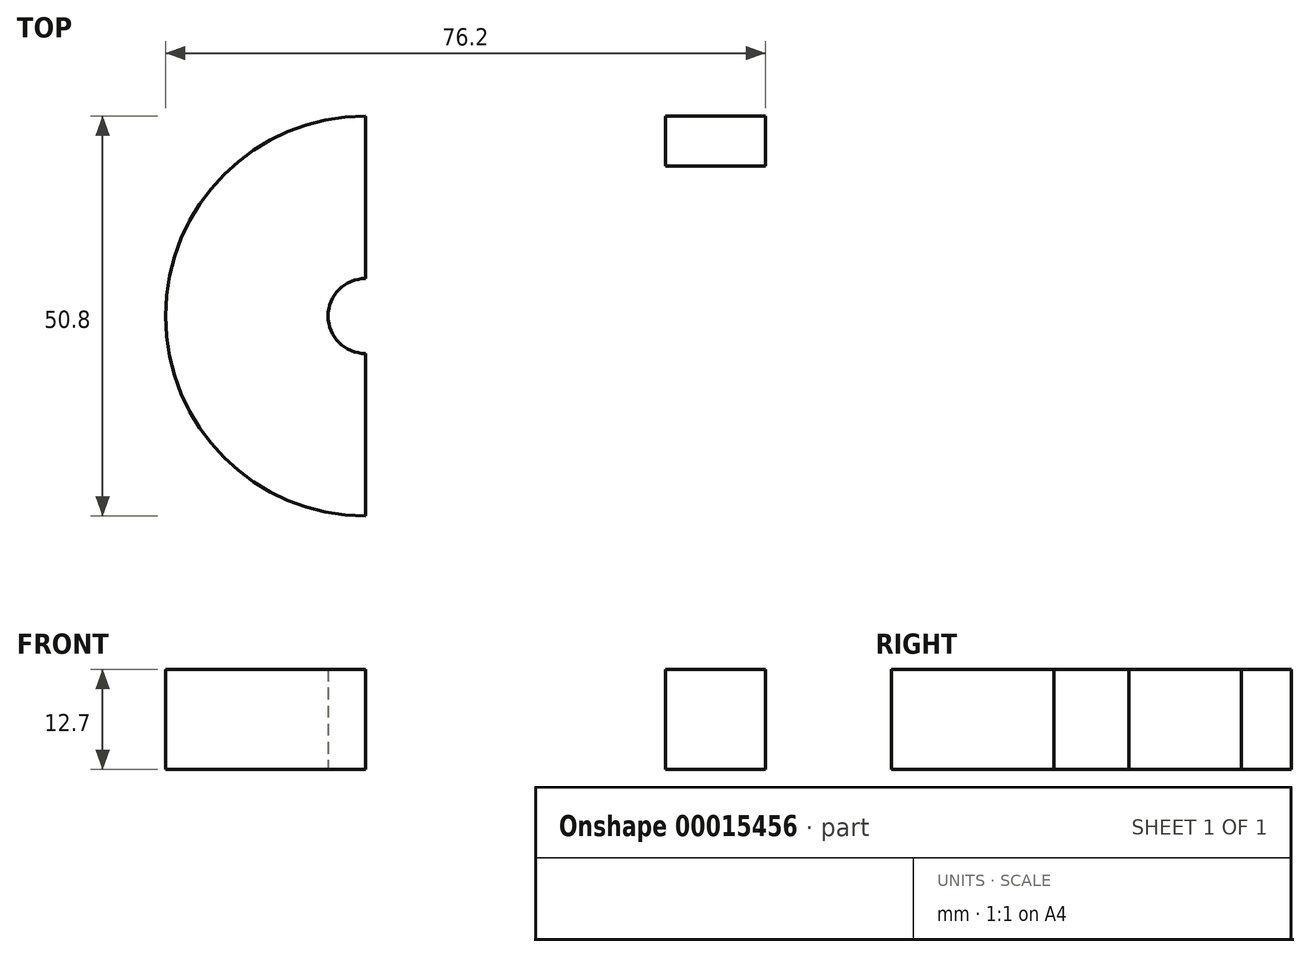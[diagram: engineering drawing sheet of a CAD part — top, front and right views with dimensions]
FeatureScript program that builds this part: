
annotation { "Feature Type Name" : "Feature", "Feature Type Description" : "" }
export const myFeature = defineFeature(function(context is Context, id is Id, definition is map)
    precondition{}
    {
        {
            var Q0;
            Q0=qCreatedBy(makeId("Top.planeOp"),FACE);
            var sketch = newSketch(context, id + "F0", { "sketchPlane" : qUnion([Q0])});
            skLineSegment(sketch, "E0.bottom", {"start": v(-6.79, 40.43) * mm, "end": v(44.01, 40.43) * mm});
            skLineSegment(sketch, "E0.top", {"start": v(-6.79, -10.37) * mm, "end": v(44.01, -10.37) * mm});
            skLineSegment(sketch, "E0.left", {"start": v(-6.79, 40.43) * mm, "end": v(-6.79, -10.37) * mm});
            skLineSegment(sketch, "E0.right", {"start": v(44.01, 40.43) * mm, "end": v(44.01, -10.37) * mm});
            skArc(sketch, "E1", {"start": v(-6.79, 40.43) * mm, "mid": v(-32.19, 15.03) * mm, "end": v(-6.79, -10.37) * mm});
            skCircle(sketch, "E2", {"center": v(-6.79, 15.03) * mm, "radius": 4.76 * mm});
            skLineSegment(sketch, "E3.bottom", {"start": v(31.31, 40.43) * mm, "end": v(44.01, 40.43) * mm});
            skLineSegment(sketch, "E3.top", {"start": v(31.31, 34.08) * mm, "end": v(44.01, 34.08) * mm});
            skLineSegment(sketch, "E3.left", {"start": v(31.31, 40.43) * mm, "end": v(31.31, 34.08) * mm});
            skLineSegment(sketch, "E3.right", {"start": v(44.01, 40.43) * mm, "end": v(44.01, 34.08) * mm});
            skLineSegment(sketch, "E4.bottom", {"start": v(31.31, -10.37) * mm, "end": v(44.01, -10.37) * mm});
            skLineSegment(sketch, "E4.top", {"start": v(31.31, -4.02) * mm, "end": v(44.01, -4.02) * mm});
            skLineSegment(sketch, "E4.left", {"start": v(31.31, -10.37) * mm, "end": v(31.31, -4.02) * mm});
            skLineSegment(sketch, "E4.right", {"start": v(44.01, -10.37) * mm, "end": v(44.01, -4.02) * mm});
            skSolve(sketch);
        }
        {
            var Q0;
            {var subQ4=sQuery(id+"F0.wireOp",EDGE,"E1");Q0=makeQuery(id+"F0.imprint","IMPRINT",FACE,{"disambiguationData":[TD([[makeQuery(id+"F0.imprint","IMPRINT",EDGE,{"derivedFrom":subQ4}),1.0]])]});}
            var Q1;
            {var subQ6=sQuery(id+"F0.wireOp",EDGE,"E0.bottom");Q1=makeQuery(id+"F0.imprint","IMPRINT",FACE,{"disambiguationData":[TD([[makeQuery(id+"F0.imprint","IMPRINT",EDGE,{"derivedFrom":subQ6}),-1.0]])]});}
            extrude(context, id + "F1", {"entities" : qUnion([Q0, Q1]), "depth" : 12.7 * mm});
        }
    });
